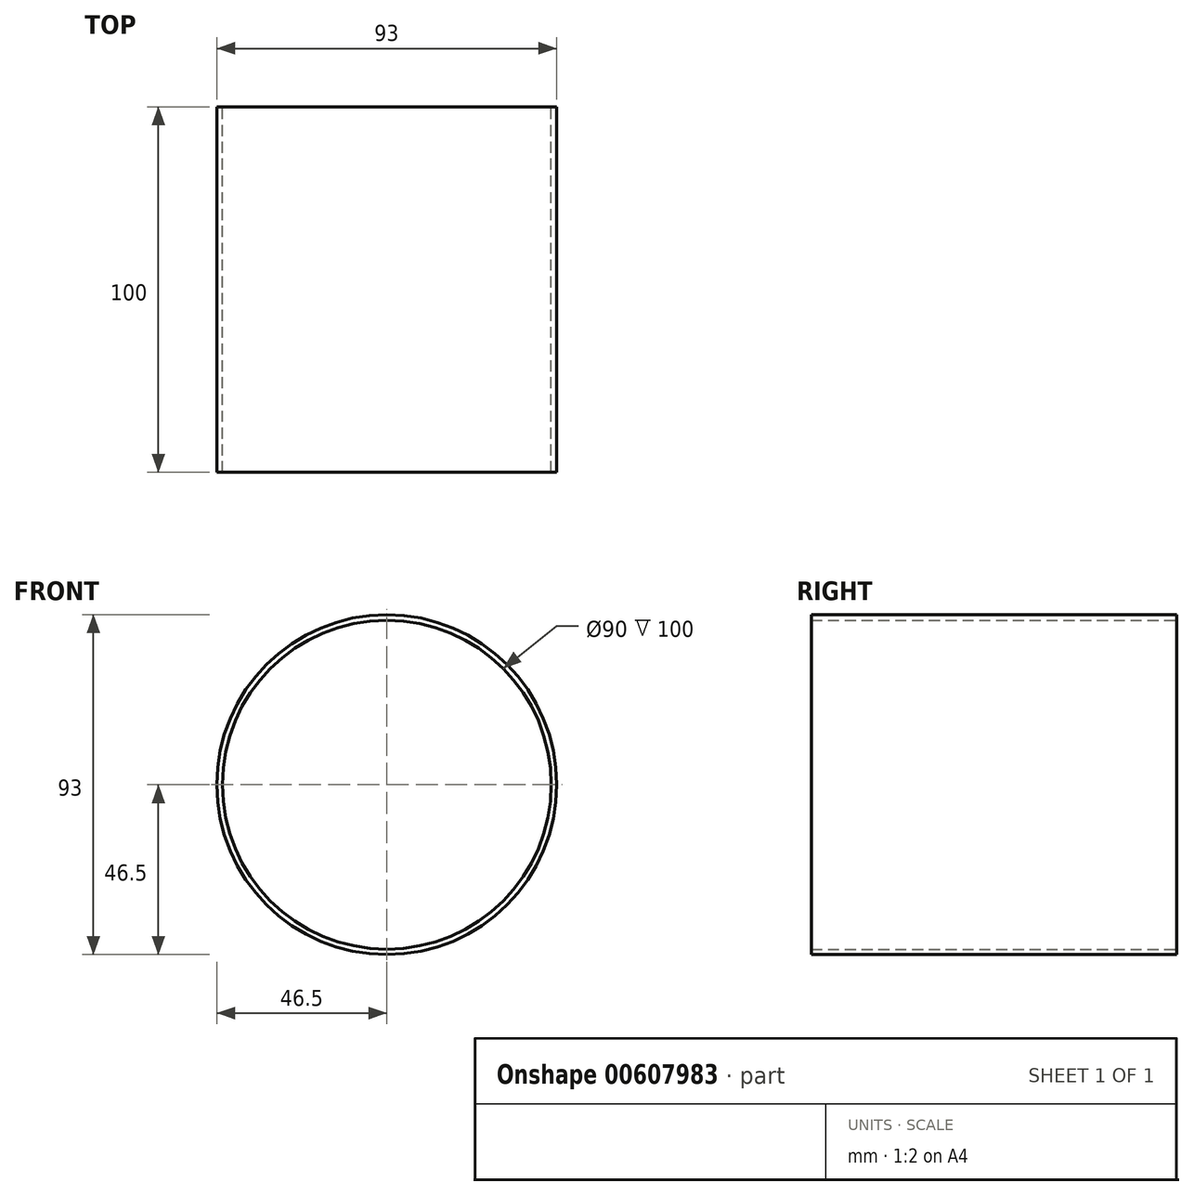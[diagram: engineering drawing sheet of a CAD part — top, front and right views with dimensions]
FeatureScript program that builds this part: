
annotation { "Feature Type Name" : "Feature", "Feature Type Description" : "" }
export const myFeature = defineFeature(function(context is Context, id is Id, definition is map)
    precondition{}
    {
        {
            var Q0;
            Q0=qCreatedBy(makeId("Front.planeOp"),FACE);
            var sketch = newSketch(context, id + "F0", { "sketchPlane" : qUnion([Q0])});
            skCircle(sketch, "E0", {"center": v(0, 0) * mm, "radius": 45 * mm});
            skCircle(sketch, "E1", {"center": v(0, 0) * mm, "radius": 46.5 * mm});
            skSolve(sketch);
        }
        {
            var Q0;
            Q0 = qSketchRegion(id + "F0", true);
            extrude(context, id + "F1", {"entities" : qUnion([Q0]), "depth" : 100 * mm, "offsetDistance" : 25 * mm});
        }
    });
